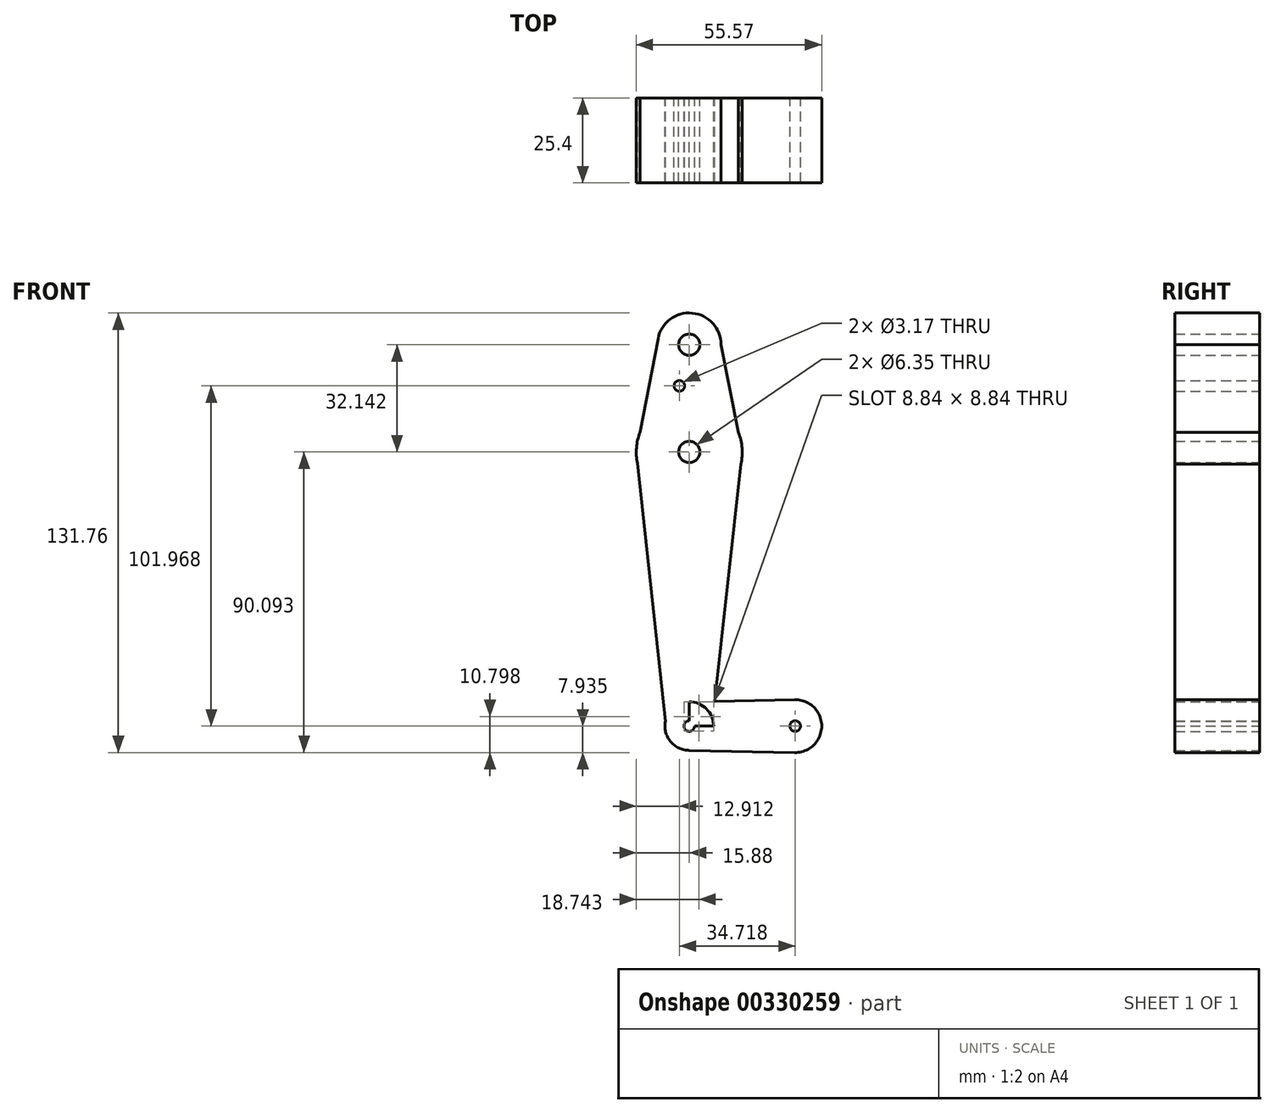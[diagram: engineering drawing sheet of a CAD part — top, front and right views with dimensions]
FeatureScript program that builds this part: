
annotation { "Feature Type Name" : "Feature", "Feature Type Description" : "" }
export const myFeature = defineFeature(function(context is Context, id is Id, definition is map)
    precondition{}
    {
        {
            var Q0;
            Q0=qCreatedBy(makeId("Front.planeOp"),FACE);
            var sketch = newSketch(context, id + "F0", { "sketchPlane" : qUnion([Q0])});
            skLineSegment(sketch, "E0", {"start": v(0, 55.21) * mm, "end": v(0, -59.09) * mm});
            skCircle(sketch, "E1", {"center": v(0, 55.21) * mm, "radius": 9.53 * mm});
            skCircle(sketch, "E2", {"center": v(0, 23.07) * mm, "radius": 15.88 * mm});
            skLineSegment(sketch, "E3", {"start": v(0, -59.09) * mm, "end": v(31.75, -59.09) * mm});
            skCircle(sketch, "E4", {"center": v(31.75, -59.09) * mm, "radius": 7.94 * mm});
            skCircle(sketch, "E5", {"center": v(0, -59.09) * mm, "radius": 7.28 * mm});
            skLineSegment(sketch, "E6", {"start": v(0, 23.07) * mm, "end": v(-63.5, 23.07) * mm});
            skLineSegment(sketch, "E7", {"start": v(9.52, 55.21) * mm, "end": v(15.87, 23.3) * mm});
            skLineSegment(sketch, "E8", {"start": v(-9.35, 57.01) * mm, "end": v(-15.87, 23.07) * mm});
            skLineSegment(sketch, "E9", {"start": v(-15.87, 23.07) * mm, "end": v(-7.14, -57.66) * mm});
            skLineSegment(sketch, "E10", {"start": v(15.87, 23.3) * mm, "end": v(6.97, -56.99) * mm});
            skLineSegment(sketch, "E11", {"start": v(0, -51.8) * mm, "end": v(31.59, -51.15) * mm});
            skLineSegment(sketch, "E12", {"start": v(0, -66.37) * mm, "end": v(31.59, -67.02) * mm});
            skCircle(sketch, "E13", {"center": v(0, 55.21) * mm, "radius": 3.18 * mm});
            skCircle(sketch, "E14", {"center": v(-2.97, 42.88) * mm, "radius": 1.59 * mm});
            skCircle(sketch, "E15", {"center": v(0, 23.07) * mm, "radius": 3.18 * mm});
            skCircle(sketch, "E16", {"center": v(0, -59.09) * mm, "radius": 1.59 * mm});
            skCircle(sketch, "E17", {"center": v(31.75, -59.09) * mm, "radius": 1.59 * mm});
            skSolve(sketch);
        }
        {
            var Q0;
            Q0 = qSketchRegion(id + "F0", true);
            extrude(context, id + "F1", {"entities" : qUnion([Q0]), "depth" : 25.4 * mm});
        }
    });
